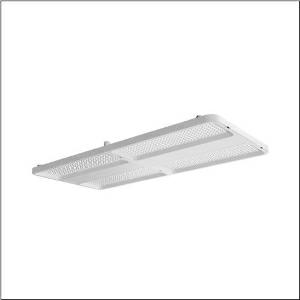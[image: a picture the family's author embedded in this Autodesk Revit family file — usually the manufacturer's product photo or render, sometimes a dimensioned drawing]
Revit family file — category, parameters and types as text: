
# Revit family: highbay_21_maxi_52hn11db5lda
name_source: partatom
category: Lighting Fixtures
units: mm (PartAtom-declared; Revit-internal decimal feet)

## family parameters
Cut with Voids When Loaded = No
Host = Face
Light Source = No
Part Type = Normal
Room Calculation Point = No
Round Connector Dimension = Use Diameter
Shared = No

## types (1)
- --- (1 x LED, 4120 lm, 22.6 W, 5000K)
    Apparent Load = 23 VA
    CIE Flux Codes = 89 97 99 100 100
    Color Rendering = 80
    Color Temperature = 5000K
    Default Elevation = 1800 mm
    Description = high bay luminaire Highbay 21 maxi; direct symmetric narrow distribution, light control with lens of PMMA; UGR ≤ 19 (X = 4H | Y = 8H | S = 0.25H | reflection values 70/50/20); luminous flux: 27.240lm; light colour: 850, colour temperature: 5000K, MacAdam ≤ 3 SDCM (initial), colour rendering: CRI > 80; luminous efficacy: 189,2lm/W; rated service life: 75.000h (L80/B50) at AT= ta max; control: DALI 2; luminaire connection: terminal, 5-pole, max. 2.5mm² (cable entry for one cable, Ø 8.5..16mm); mains connection: 230..240V, AC/DC 0/50..60Hz; connected load: 144W; protection rating (complete): IP66; insulation class (complete): insulation class I (protective earthing); protection symbol: D; impact resistance: IK08; certification: CE, ENEC, VDE, UKCA; luminaire for central battery installations according to DIN EN 60598-2-22, internal wiring halogen-free; luminaire corresponds to IFS (International Featured Standards) requirements for safety and quality in the food industry; LABS conformity tested according to VDMA 24364:2018-05; housing frame of high-performance plastic PA6, matt traffic white (RAL 9016); cover of PMMA; dimension (LxWxH): 946 x 442 x 72mm; permissible operating ambient temperature: -40..+65°C (reducing of maximum allowable ambient temperature of 5°C with ceiling mounting); packaging unit: 1 piece; (delivery without accessories; please order mounting accessories separately)
    Height = 72 mm  [stored 0.23622 ft]
    Lamp = 1 x LED
    Lamp Light Flux = 4120 lm
    Lamp Power = 22.6 W
    Lamp count = 1
    Length = 946 mm
    Luminous efficacy = 182 lm/W
    Manufacturer = Siteco
    ModVariant = No
    Model = 52HN11DB5LDA
    Mounting Place = Ceiling
    Mounting Type = Pendant
    Number of Poles = 1
    OnlyDefault = Yes
    Power Factor = 1
    Product Name = Highbay 21 maxi
    Product group = high bay luminaire
    ProductGroupID = 901
    Protection Class = Protection class I
    Protection Degree = IP 66
    RLX_Detail_Level = 1
    RLX_Emergency_Light_Flux = 0 lm
    RLX_Emergency_Type = 0
    RLX_Emergency_Type_DB = No
    RlxData = <blob elided: 127861 chars, md5=432541e9>
    Socket = socket
    Standby Power = 0 W
    System Light Flux = 4120 lm
    System Power = 23 W
    Type Comments = : DC mode (central or group accumulator) initial emergency light level
    Type Image = l_1363244.jpg
    URL = http://relux.com
    VarID = @adj_001003
    Voltage = 0 V
    Weight = 0.00 kg
    Width = 442 mm

note: [stored X ft] marks values corroborated as IEEE doubles in the binary element streams (Revit-internal decimal feet)

## geometry (parser evidence)
native form markers: Blend x4, Sweep x11
no freeform markers — native parametric forms only
